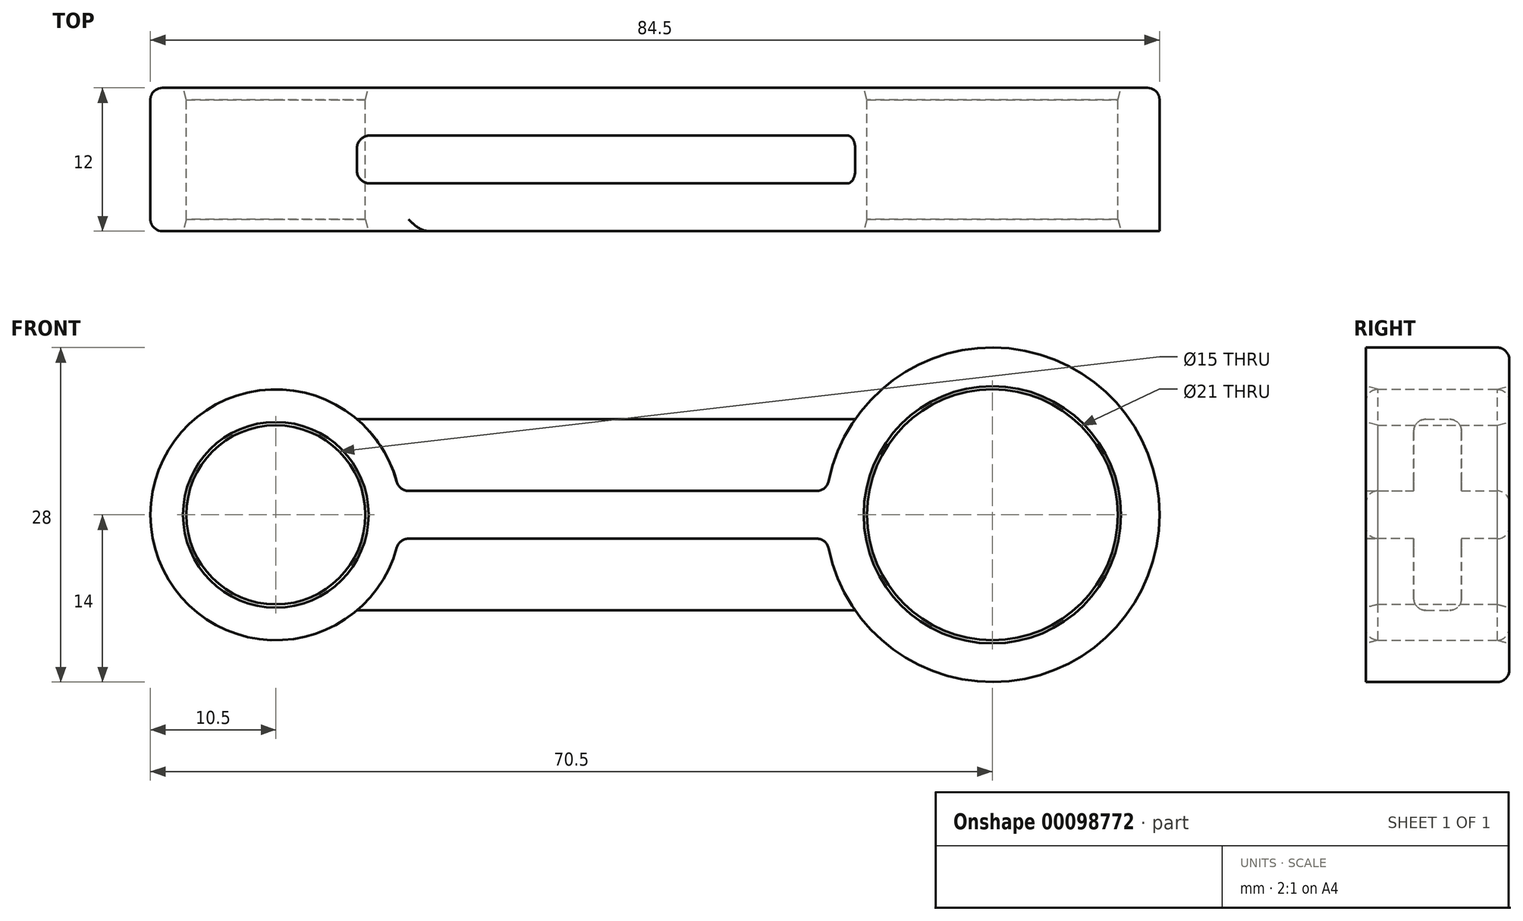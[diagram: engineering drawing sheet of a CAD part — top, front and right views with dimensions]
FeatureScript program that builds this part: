
annotation { "Feature Type Name" : "Feature", "Feature Type Description" : "" }
export const myFeature = defineFeature(function(context is Context, id is Id, definition is map)
    precondition{}
    {
        {
            var Q0;
            Q0=qCreatedBy(makeId("Front.planeOp"),FACE);
            var sketch = newSketch(context, id + "F0", { "sketchPlane" : qUnion([Q0])});
            skCircle(sketch, "E0", {"center": v(0, 0) * mm, "radius": 10.5 * mm});
            skCircle(sketch, "E1", {"center": v(0, 0) * mm, "radius": 14 * mm});
            skCircle(sketch, "E2", {"center": v(-60, 0) * mm, "radius": 7.5 * mm});
            skCircle(sketch, "E3", {"center": v(-60, 0) * mm, "radius": 10.5 * mm});
            skLineSegment(sketch, "E4", {"start": v(-53.2, 8) * mm, "end": v(-11.49, 8) * mm});
            skLineSegment(sketch, "E5", {"start": v(-53.2, -8) * mm, "end": v(-11.49, -8) * mm});
            skLineSegment(sketch, "E6", {"start": v(-49.7, 2) * mm, "end": v(-13.86, 2) * mm});
            skLineSegment(sketch, "E7", {"start": v(-49.7, -2) * mm, "end": v(-13.86, -2) * mm});
            skSolve(sketch);
        }
        {
            var Q0;
            Q0=makeQuery(id+"F0.imprint","IMPRINT",FACE,{"disambiguationData":[TD([[makeQuery(id+"F0.imprint","IMPRINT",EDGE,{"derivedFrom":sQuery(id+"F0.wireOp",EDGE,"E2")}),-1.0]])]});
            var Q1;
            Q1=makeQuery(id+"F0.imprint","IMPRINT",FACE,{"disambiguationData":[TD([[makeQuery(id+"F0.imprint","IMPRINT",EDGE,{"derivedFrom":sQuery(id+"F0.wireOp",EDGE,"E0")}),-1.0]])]});
            var Q2;
            {var subQ0=sQuery(id+"F0.wireOp",EDGE,"E6");Q2=makeQuery(id+"F0.imprint","IMPRINT",FACE,{"disambiguationData":[TD([[makeQuery(id+"F0.imprint","IMPRINT",EDGE,{"derivedFrom":subQ0}),-1.0]])]});}
            extrude(context, id + "F1", {"entities" : qUnion([Q0, Q1, Q2]), "offsetDistance" : 25 * mm, "depth" : 12 * mm, "symmetric" : true});
        }
        {
            var Q0;
            {var subQ0=sQuery(id+"F0.wireOp",EDGE,"E4");Q0=makeQuery(id+"F0.imprint","IMPRINT",FACE,{"disambiguationData":[TD([[makeQuery(id+"F0.imprint","IMPRINT",EDGE,{"derivedFrom":subQ0}),-1.0]])]});}
            var Q1;
            {var subQ0=sQuery(id+"F0.wireOp",EDGE,"E5");Q1=makeQuery(id+"F0.imprint","IMPRINT",FACE,{"disambiguationData":[TD([[makeQuery(id+"F0.imprint","IMPRINT",EDGE,{"derivedFrom":subQ0}),1.0]])]});}
            extrude(context, id + "F2", {"entities" : qUnion([Q0, Q1]), "operationType" : NewBodyOperationType.ADD, "offsetDistance" : 25 * mm, "depth" : 4 * mm, "symmetric" : true});
        }
        {
            var Q0;
            Q0=makeQuery(id+"F1.opExtrude","CAP_EDGE",EDGE,{"disambiguationData":[OSD([sQuery(id+"F0.wireOp",EDGE,"E2")])],"isStart":false});
            var Q1;
            Q1=makeQuery(id+"F1.opExtrude","CAP_EDGE",EDGE,{"disambiguationData":[OSD([sQuery(id+"F0.wireOp",EDGE,"E0")])],"isStart":false});
            chamfer(context, id + "F3", {"entities" : qUnion([Q0, Q1]), "chamferType" : ChamferType.OFFSET_ANGLE, "width" : 1 * mm, "oppositeDirection" : false, "angle" : 15 * degree, "tangentPropagation" : true});
        }
        {
            var Q0;
            Q0=makeQuery(id+"F1.opExtrude","CAP_EDGE",EDGE,{"disambiguationData":[OSD([sQuery(id+"F0.wireOp",EDGE,"E0")])],"isStart":true});
            var Q1;
            Q1=makeQuery(id+"F1.opExtrude","CAP_EDGE",EDGE,{"disambiguationData":[OSD([sQuery(id+"F0.wireOp",EDGE,"E2")])],"isStart":true});
            chamfer(context, id + "F4", {"entities" : qUnion([Q0, Q1]), "chamferType" : ChamferType.OFFSET_ANGLE, "width" : 1 * mm, "oppositeDirection" : true, "angle" : 15 * degree, "tangentPropagation" : true});
        }
        {
            var Q0;
            {var subQ0=sQuery(id+"F0.wireOp",EDGE,"E3");Q0=makeQuery(id+"F2.opExtrude","CAP_EDGE",EDGE,{"disambiguationData":[OSD([subQ0]),TDD([makeQuery(id+"F0.imprint","IMPRINT",EDGE,{"disambiguationData":[TD([[makeQuery(id+"F0.imprint","INTERSECT",VERTEX,{"derivedFrom":[subQ0,sQuery(id+"F0.wireOp",EDGE,"E4")]}),1.0]])],"derivedFrom":subQ0})])],"isStart":false});}
            var Q1;
            Q1=makeQuery(id+"F2.opExtrude","CAP_EDGE",EDGE,{"disambiguationData":[OSD([sQuery(id+"F0.wireOp",EDGE,"E6")])],"isStart":false});
            var Q2;
            {var subQ0=sQuery(id+"F0.wireOp",EDGE,"E6");var subQ1=sQuery(id+"F0.wireOp",EDGE,"E3");var subQ2=sQuery(id+"F0.wireOp",EDGE,"E1");Q2=makeQuery(id+"F2.boolean.opBoolean","SPLIT",EDGE,{"disambiguationData":[TD([makeQuery(id+"F2.opExtrude","CAP_FACE",FACE,{"disambiguationData":[OSD([subQ2,subQ1,sQuery(id+"F0.wireOp",EDGE,"E4"),subQ0])],"isStart":false})])],"derivedFrom":makeQuery(id+"F1.opExtrude","SWEPT_EDGE",EDGE,{"disambiguationData":[OSD([subQ1,subQ0])]})});}
            var Q3;
            {var subQ0=sQuery(id+"F0.wireOp",EDGE,"E1");Q3=makeQuery(id+"F2.opExtrude","CAP_EDGE",EDGE,{"disambiguationData":[OSD([subQ0]),TDD([makeQuery(id+"F0.imprint","IMPRINT",EDGE,{"disambiguationData":[TD([[makeQuery(id+"F0.imprint","INTERSECT",VERTEX,{"derivedFrom":[subQ0,sQuery(id+"F0.wireOp",EDGE,"E4")]}),-1.0]])],"derivedFrom":subQ0})])],"isStart":false});}
            var Q4;
            {var subQ0=sQuery(id+"F0.wireOp",EDGE,"E6");var subQ1=sQuery(id+"F0.wireOp",EDGE,"E3");var subQ2=sQuery(id+"F0.wireOp",EDGE,"E1");Q4=makeQuery(id+"F2.boolean.opBoolean","SPLIT",EDGE,{"disambiguationData":[TD([makeQuery(id+"F2.opExtrude","CAP_FACE",FACE,{"disambiguationData":[OSD([subQ2,subQ1,sQuery(id+"F0.wireOp",EDGE,"E4"),subQ0])],"isStart":false})])],"derivedFrom":makeQuery(id+"F1.opExtrude","SWEPT_EDGE",EDGE,{"disambiguationData":[OSD([subQ2,subQ0])]})});}
            var Q5;
            Q5=makeQuery(id+"F2.opExtrude","CAP_EDGE",EDGE,{"disambiguationData":[OSD([sQuery(id+"F0.wireOp",EDGE,"E7")])],"isStart":false});
            var Q6;
            {var subQ0=sQuery(id+"F0.wireOp",EDGE,"E1");Q6=makeQuery(id+"F2.opExtrude","CAP_EDGE",EDGE,{"disambiguationData":[OSD([subQ0]),TDD([makeQuery(id+"F0.imprint","IMPRINT",EDGE,{"disambiguationData":[TD([[makeQuery(id+"F0.imprint","INTERSECT",VERTEX,{"derivedFrom":[subQ0,sQuery(id+"F0.wireOp",EDGE,"E5")]}),1.0]])],"derivedFrom":subQ0})])],"isStart":false});}
            var Q7;
            {var subQ0=sQuery(id+"F0.wireOp",EDGE,"E7");var subQ1=sQuery(id+"F0.wireOp",EDGE,"E3");var subQ2=sQuery(id+"F0.wireOp",EDGE,"E1");Q7=makeQuery(id+"F2.boolean.opBoolean","SPLIT",EDGE,{"disambiguationData":[TD([makeQuery(id+"F2.opExtrude","CAP_FACE",FACE,{"disambiguationData":[OSD([subQ2,subQ1,sQuery(id+"F0.wireOp",EDGE,"E5"),subQ0])],"isStart":false})])],"derivedFrom":makeQuery(id+"F1.opExtrude","SWEPT_EDGE",EDGE,{"disambiguationData":[OSD([subQ2,subQ0])]})});}
            var Q8;
            {var subQ0=sQuery(id+"F0.wireOp",EDGE,"E7");var subQ1=sQuery(id+"F0.wireOp",EDGE,"E3");var subQ2=sQuery(id+"F0.wireOp",EDGE,"E1");Q8=makeQuery(id+"F2.boolean.opBoolean","SPLIT",EDGE,{"disambiguationData":[TD([makeQuery(id+"F2.opExtrude","CAP_FACE",FACE,{"disambiguationData":[OSD([subQ2,subQ1,sQuery(id+"F0.wireOp",EDGE,"E5"),subQ0])],"isStart":false})])],"derivedFrom":makeQuery(id+"F1.opExtrude","SWEPT_EDGE",EDGE,{"disambiguationData":[OSD([subQ1,subQ0])]})});}
            var Q9;
            {var subQ0=sQuery(id+"F0.wireOp",EDGE,"E3");Q9=makeQuery(id+"F2.opExtrude","CAP_EDGE",EDGE,{"disambiguationData":[OSD([subQ0]),TDD([makeQuery(id+"F0.imprint","IMPRINT",EDGE,{"disambiguationData":[TD([[makeQuery(id+"F0.imprint","INTERSECT",VERTEX,{"derivedFrom":[subQ0,sQuery(id+"F0.wireOp",EDGE,"E5")]}),-1.0]])],"derivedFrom":subQ0})])],"isStart":false});}
            var Q10;
            Q10=makeQuery(id+"F2.opExtrude","CAP_EDGE",EDGE,{"disambiguationData":[OSD([sQuery(id+"F0.wireOp",EDGE,"E5")])],"isStart":false});
            var Q11;
            Q11=makeQuery(id+"F2.opExtrude","CAP_EDGE",EDGE,{"disambiguationData":[OSD([sQuery(id+"F0.wireOp",EDGE,"E4")])],"isStart":false});
            var Q12;
            Q12=makeQuery(id+"F1.opExtrude","CAP_EDGE",EDGE,{"disambiguationData":[OSD([sQuery(id+"F0.wireOp",EDGE,"E3")])],"isStart":false});
            fillet(context, id + "F5", {"entities" : qUnion([Q0, Q1, Q2, Q3, Q4, Q5, Q6, Q7, Q8, Q9, Q10, Q11, Q12]), "radius" : 1 * mm, "tangentPropagation" : true, "allowEdgeOverflow" : false});
        }
        {
            var Q0;
            Q0=makeQuery(id+"F1.opExtrude","CAP_EDGE",EDGE,{"disambiguationData":[OSD([sQuery(id+"F0.wireOp",EDGE,"E1")])],"isStart":true});
            var Q1;
            Q1=makeQuery(id+"F1.opExtrude","CAP_EDGE",EDGE,{"disambiguationData":[OSD([sQuery(id+"F0.wireOp",EDGE,"E6")])],"isStart":true});
            var Q2;
            Q2=makeQuery(id+"F1.opExtrude","CAP_EDGE",EDGE,{"disambiguationData":[OSD([sQuery(id+"F0.wireOp",EDGE,"E7")])],"isStart":true});
            var Q3;
            Q3=makeQuery(id+"F1.opExtrude","CAP_EDGE",EDGE,{"disambiguationData":[OSD([sQuery(id+"F0.wireOp",EDGE,"E3")])],"isStart":true});
            var Q4;
            Q4=makeQuery(id+"F2.opExtrude","CAP_EDGE",EDGE,{"disambiguationData":[OSD([sQuery(id+"F0.wireOp",EDGE,"E6")])],"isStart":true});
            var Q5;
            {var subQ0=sQuery(id+"F0.wireOp",EDGE,"E3");Q5=makeQuery(id+"F2.opExtrude","CAP_EDGE",EDGE,{"disambiguationData":[OSD([subQ0]),TDD([makeQuery(id+"F0.imprint","IMPRINT",EDGE,{"disambiguationData":[TD([[makeQuery(id+"F0.imprint","INTERSECT",VERTEX,{"derivedFrom":[subQ0,sQuery(id+"F0.wireOp",EDGE,"E4")]}),1.0]])],"derivedFrom":subQ0})])],"isStart":true});}
            var Q6;
            {var subQ0=sQuery(id+"F0.wireOp",EDGE,"E6");var subQ1=sQuery(id+"F0.wireOp",EDGE,"E3");var subQ2=sQuery(id+"F0.wireOp",EDGE,"E1");Q6=makeQuery(id+"F2.boolean.opBoolean","SPLIT",EDGE,{"disambiguationData":[TD([makeQuery(id+"F2.opExtrude","CAP_FACE",FACE,{"disambiguationData":[OSD([subQ2,subQ1,sQuery(id+"F0.wireOp",EDGE,"E4"),subQ0])],"isStart":true})])],"derivedFrom":makeQuery(id+"F1.opExtrude","SWEPT_EDGE",EDGE,{"disambiguationData":[OSD([subQ1,subQ0])]})});}
            var Q7;
            Q7=makeQuery(id+"F2.opExtrude","CAP_EDGE",EDGE,{"disambiguationData":[OSD([sQuery(id+"F0.wireOp",EDGE,"E4")])],"isStart":true});
            var Q8;
            {var subQ0=sQuery(id+"F0.wireOp",EDGE,"E1");Q8=makeQuery(id+"F2.opExtrude","CAP_EDGE",EDGE,{"disambiguationData":[OSD([subQ0]),TDD([makeQuery(id+"F0.imprint","IMPRINT",EDGE,{"disambiguationData":[TD([[makeQuery(id+"F0.imprint","INTERSECT",VERTEX,{"derivedFrom":[subQ0,sQuery(id+"F0.wireOp",EDGE,"E4")]}),-1.0]])],"derivedFrom":subQ0})])],"isStart":true});}
            var Q9;
            {var subQ0=sQuery(id+"F0.wireOp",EDGE,"E6");var subQ1=sQuery(id+"F0.wireOp",EDGE,"E3");var subQ2=sQuery(id+"F0.wireOp",EDGE,"E1");Q9=makeQuery(id+"F2.boolean.opBoolean","SPLIT",EDGE,{"disambiguationData":[TD([makeQuery(id+"F2.opExtrude","CAP_FACE",FACE,{"disambiguationData":[OSD([subQ2,subQ1,sQuery(id+"F0.wireOp",EDGE,"E4"),subQ0])],"isStart":true})])],"derivedFrom":makeQuery(id+"F1.opExtrude","SWEPT_EDGE",EDGE,{"disambiguationData":[OSD([subQ2,subQ0])]})});}
            var Q10;
            Q10=makeQuery(id+"F2.opExtrude","CAP_EDGE",EDGE,{"disambiguationData":[OSD([sQuery(id+"F0.wireOp",EDGE,"E7")])],"isStart":true});
            var Q11;
            {var subQ0=sQuery(id+"F0.wireOp",EDGE,"E7");var subQ1=sQuery(id+"F0.wireOp",EDGE,"E3");var subQ2=sQuery(id+"F0.wireOp",EDGE,"E1");Q11=makeQuery(id+"F2.boolean.opBoolean","SPLIT",EDGE,{"disambiguationData":[TD([makeQuery(id+"F2.opExtrude","CAP_FACE",FACE,{"disambiguationData":[OSD([subQ2,subQ1,sQuery(id+"F0.wireOp",EDGE,"E5"),subQ0])],"isStart":true})])],"derivedFrom":makeQuery(id+"F1.opExtrude","SWEPT_EDGE",EDGE,{"disambiguationData":[OSD([subQ1,subQ0])]})});}
            var Q12;
            {var subQ0=sQuery(id+"F0.wireOp",EDGE,"E3");Q12=makeQuery(id+"F2.opExtrude","CAP_EDGE",EDGE,{"disambiguationData":[OSD([subQ0]),TDD([makeQuery(id+"F0.imprint","IMPRINT",EDGE,{"disambiguationData":[TD([[makeQuery(id+"F0.imprint","INTERSECT",VERTEX,{"derivedFrom":[subQ0,sQuery(id+"F0.wireOp",EDGE,"E5")]}),-1.0]])],"derivedFrom":subQ0})])],"isStart":true});}
            var Q13;
            Q13=makeQuery(id+"F2.opExtrude","CAP_EDGE",EDGE,{"disambiguationData":[OSD([sQuery(id+"F0.wireOp",EDGE,"E5")])],"isStart":true});
            var Q14;
            {var subQ0=sQuery(id+"F0.wireOp",EDGE,"E1");Q14=makeQuery(id+"F2.opExtrude","CAP_EDGE",EDGE,{"disambiguationData":[OSD([subQ0]),TDD([makeQuery(id+"F0.imprint","IMPRINT",EDGE,{"disambiguationData":[TD([[makeQuery(id+"F0.imprint","INTERSECT",VERTEX,{"derivedFrom":[subQ0,sQuery(id+"F0.wireOp",EDGE,"E5")]}),1.0]])],"derivedFrom":subQ0})])],"isStart":true});}
            var Q15;
            {var subQ0=sQuery(id+"F0.wireOp",EDGE,"E7");var subQ1=sQuery(id+"F0.wireOp",EDGE,"E3");var subQ2=sQuery(id+"F0.wireOp",EDGE,"E1");Q15=makeQuery(id+"F2.boolean.opBoolean","SPLIT",EDGE,{"disambiguationData":[TD([makeQuery(id+"F2.opExtrude","CAP_FACE",FACE,{"disambiguationData":[OSD([subQ2,subQ1,sQuery(id+"F0.wireOp",EDGE,"E5"),subQ0])],"isStart":true})])],"derivedFrom":makeQuery(id+"F1.opExtrude","SWEPT_EDGE",EDGE,{"disambiguationData":[OSD([subQ2,subQ0])]})});}
            fillet(context, id + "F6", {"entities" : qUnion([Q0, Q1, Q2, Q3, Q4, Q5, Q6, Q7, Q8, Q9, Q10, Q11, Q12, Q13, Q14, Q15]), "radius" : 1 * mm, "tangentPropagation" : true, "allowEdgeOverflow" : false});
        }
    });
